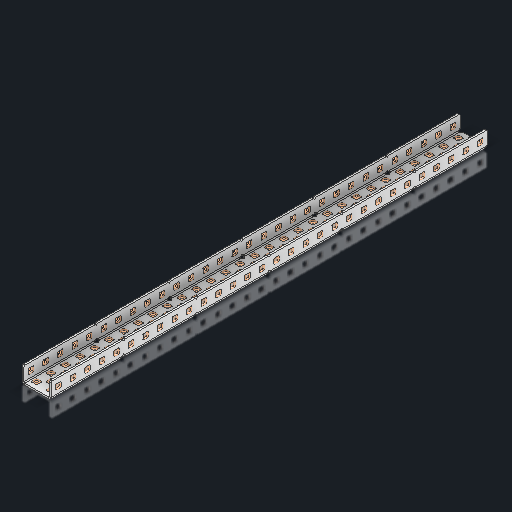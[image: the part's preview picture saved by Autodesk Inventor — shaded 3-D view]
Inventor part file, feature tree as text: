
AUTODESK INVENTOR PART (.ipt)
format: ipt  version: 2023.2 (Build 272271030, 271C)  size: 2,641,920 bytes
history: native  units: in
note: dims shown in document units (in); Inventor stores cm internally (conversion verified against a paired STEP export)
features: other x306, sketch x10, sheet_metal_op x1
ambient origin geometry x8: Origin, YZ Plane, XZ Plane, XY Plane, X Axis, Y Axis, Z Axis, Center Point
bodies: Solid1 (feature_tree)
feature tree (317):
  other  "Alu C 1x2x1x30_MIR.ipt"
  other  "Solid1::Alu C 1x2x1x30_MIR.ipt"
  other  "TaggingFeature1"
  sketch  "Sketch1"  dims[d0=0.3937in]
  sketch  "Sketch2"  dims[d1=0.0625in]
  sketch  "Sketch3"
  sketch  "Sketch7"
  other  "Flange Pattern Sketch"
  sketch  "Sketch8"
  sketch  "Sketch9"
  sheet_metal_op  "Body Pattern Sketch"
  sketch  "Sketch15"
  sketch  "Sketch16"
  other  "Arc Length"
  sketch  "Sketch13"
  sketch  "Sketch14"
  other  "Flange Pattern Plane"
  other  "Srf1"
  other  "Srf2"
  other  "Srf3"
  other  "Srf4"
  other  "Srf5"
  other  "Srf6"
  other  "Srf7"
  other  "Srf8"
  other  "Srf9"
  other  "Srf10"
  other  "Srf11"
  other  "Srf12"
  other  "Srf13"
  other  "Srf14"
  other  "Srf15"
  other  "Srf16"
  other  "Srf17"
  other  "Srf18"
  other  "Srf19"
  other  "Srf20"
  other  "Srf21"
  other  "Srf22"
  other  "Srf23"
  other  "Srf24"
  other  "Srf25"
  other  "Srf26"
  other  "Srf27"
  other  "Srf28"
  other  "Srf29"
  other  "Srf30"
  other  "Srf31"
  other  "Srf32"
  other  "Srf33"
  other  "Srf34"
  other  "Srf35"
  other  "Srf36"
  other  "Srf37"
  other  "Srf38"
  other  "Srf39"
  other  "Srf40"
  other  "Srf41"
  other  "Srf42"
  other  "Srf43"
  other  "Srf44"
  other  "Srf45"
  other  "Srf46"
  other  "Srf47"
  other  "Srf48"
  other  "Srf49"
  other  "Srf50"
  other  "Srf51"
  other  "Srf52"
  other  "Srf53"
  other  "Srf54"
  other  "Srf55"
  other  "Srf56"
  other  "Srf57"
  other  "Srf58"
  other  "Srf59"
  other  "Srf60"
  other  "Srf61"
  other  "Srf62"
  other  "Srf63"
  other  "Srf64"
  other  "Srf65"
  other  "Srf66"
  other  "Srf67"
  other  "Srf68"
  other  "Srf69"
  other  "Srf70"
  other  "Srf71"
  other  "Srf72"
  other  "Srf73"
  other  "Srf74"
  other  "Srf75"
  other  "Srf76"
  other  "Srf77"
  other  "Srf78"
  other  "Srf79"
  other  "Srf80"
  other  "Srf81"
  other  "Srf82"
  other  "Srf83"
  other  "Srf84"
  other  "Srf85"
  other  "Srf86"
  other  "Srf87"
  other  "Srf88"
  other  "Srf89"
  other  "Srf90"
  other  "Srf91"
  other  "Srf92"
  other  "Srf93"
  other  "Srf94"
  other  "Srf95"
  other  "Srf96"
  other  "Srf97"
  other  "Srf98"
  other  "Srf99"
  other  "Srf100"
  other  "Srf101"
  other  "Srf102"
  other  "Srf103"
  other  "Srf104"
  other  "Srf105"
  other  "Srf106"
  other  "Srf107"
  other  "Srf108"
  other  "Srf109"
  other  "Srf110"
  other  "Srf111"
  other  "Srf112"
  other  "Srf113"
  other  "Srf114"
  other  "Srf115"
  other  "Srf116"
  other  "Srf117"
  other  "Srf118"
  other  "Srf119"
  other  "Srf120"
  other  "Srf121"
  other  "Srf122"
  other  "Srf123"
  other  "Srf124"
  other  "Srf125"
  other  "Srf126"
  other  "Srf127"
  other  "Srf128"
  other  "Srf129"
  other  "Srf130"
  other  "Srf131"
  other  "Srf132"
  other  "Srf133"
  other  "Srf134"
  other  "Srf135"
  other  "Srf136"
  other  "Srf137"
  other  "Srf138"
  other  "Srf139"
  other  "Srf140"
  other  "Srf141"
  other  "Srf142"
  other  "Srf143"
  other  "Srf144"
  other  "Srf145"
  other  "Srf146"
  other  "Srf147"
  other  "Srf148"
  other  "Srf149"
  other  "Srf150"
  other  "Srf1::Derived"
  other  "Srf2::Derived"
  other  "Srf3::Derived"
  other  "Srf4::Derived"
  other  "Srf5::Derived"
  other  "Srf6::Derived"
  other  "Srf7::Derived"
  other  "Srf8::Derived"
  other  "Srf9::Derived"
  other  "Srf10::Derived"
  other  "Srf11::Derived"
  other  "Srf12::Derived"
  other  "Srf13::Derived"
  other  "Srf14::Derived"
  other  "Srf15::Derived"
  other  "Srf16::Derived"
  other  "Srf17::Derived"
  other  "Srf18::Derived"
  other  "Srf19::Derived"
  other  "Srf20::Derived"
  other  "Srf21::Derived"
  other  "Srf22::Derived"
  other  "Srf23::Derived"
  other  "Srf24::Derived"
  other  "Srf25::Derived"
  other  "Srf26::Derived"
  other  "Srf27::Derived"
  other  "Srf28::Derived"
  other  "Srf29::Derived"
  other  "Srf30::Derived"
  other  "Srf31::Derived"
  other  "Srf32::Derived"
  other  "Srf33::Derived"
  other  "Srf34::Derived"
  other  "Srf35::Derived"
  other  "Srf36::Derived"
  other  "Srf37::Derived"
  other  "Srf38::Derived"
  other  "Srf39::Derived"
  other  "Srf40::Derived"
  other  "Srf41::Derived"
  other  "Srf42::Derived"
  other  "Srf43::Derived"
  other  "Srf44::Derived"
  other  "Srf45::Derived"
  other  "Srf46::Derived"
  other  "Srf47::Derived"
  other  "Srf48::Derived"
  other  "Srf49::Derived"
  other  "Srf50::Derived"
  other  "Srf51::Derived"
  other  "Srf52::Derived"
  other  "Srf53::Derived"
  other  "Srf54::Derived"
  other  "Srf55::Derived"
  other  "Srf56::Derived"
  other  "Srf57::Derived"
  other  "Srf58::Derived"
  other  "Srf59::Derived"
  other  "Srf60::Derived"
  other  "Srf61::Derived"
  other  "Srf62::Derived"
  other  "Srf63::Derived"
  other  "Srf64::Derived"
  other  "Srf65::Derived"
  other  "Srf66::Derived"
  other  "Srf67::Derived"
  other  "Srf68::Derived"
  other  "Srf69::Derived"
  other  "Srf70::Derived"
  other  "Srf71::Derived"
  other  "Srf72::Derived"
  other  "Srf73::Derived"
  other  "Srf74::Derived"
  other  "Srf75::Derived"
  other  "Srf76::Derived"
  other  "Srf77::Derived"
  other  "Srf78::Derived"
  other  "Srf79::Derived"
  other  "Srf80::Derived"
  other  "Srf81::Derived"
  other  "Srf82::Derived"
  other  "Srf83::Derived"
  other  "Srf84::Derived"
  other  "Srf85::Derived"
  other  "Srf86::Derived"
  other  "Srf87::Derived"
  other  "Srf88::Derived"
  other  "Srf89::Derived"
  other  "Srf90::Derived"
  other  "Srf91::Derived"
  other  "Srf92::Derived"
  other  "Srf93::Derived"
  other  "Srf94::Derived"
  other  "Srf95::Derived"
  other  "Srf96::Derived"
  other  "Srf97::Derived"
  other  "Srf98::Derived"
  other  "Srf99::Derived"
  other  "Srf100::Derived"
  other  "Srf101::Derived"
  other  "Srf102::Derived"
  other  "Srf103::Derived"
  other  "Srf104::Derived"
  other  "Srf105::Derived"
  other  "Srf106::Derived"
  other  "Srf107::Derived"
  other  "Srf108::Derived"
  other  "Srf109::Derived"
  other  "Srf110::Derived"
  other  "Srf111::Derived"
  other  "Srf112::Derived"
  other  "Srf113::Derived"
  other  "Srf114::Derived"
  other  "Srf115::Derived"
  other  "Srf116::Derived"
  other  "Srf117::Derived"
  other  "Srf118::Derived"
  other  "Srf119::Derived"
  other  "Srf120::Derived"
  other  "Srf121::Derived"
  other  "Srf122::Derived"
  other  "Srf123::Derived"
  other  "Srf124::Derived"
  other  "Srf125::Derived"
  other  "Srf126::Derived"
  other  "Srf127::Derived"
  other  "Srf128::Derived"
  other  "Srf129::Derived"
  other  "Srf130::Derived"
  other  "Srf131::Derived"
  other  "Srf132::Derived"
  other  "Srf133::Derived"
  other  "Srf134::Derived"
  other  "Srf135::Derived"
  other  "Srf136::Derived"
  other  "Srf137::Derived"
  other  "Srf138::Derived"
  other  "Srf139::Derived"
  other  "Srf140::Derived"
  other  "Srf141::Derived"
  other  "Srf142::Derived"
  other  "Srf143::Derived"
  other  "Srf144::Derived"
  other  "Srf145::Derived"
  other  "Srf146::Derived"
  other  "Srf147::Derived"
  other  "Srf148::Derived"
  other  "Srf149::Derived"
  other  "Srf150::Derived"
